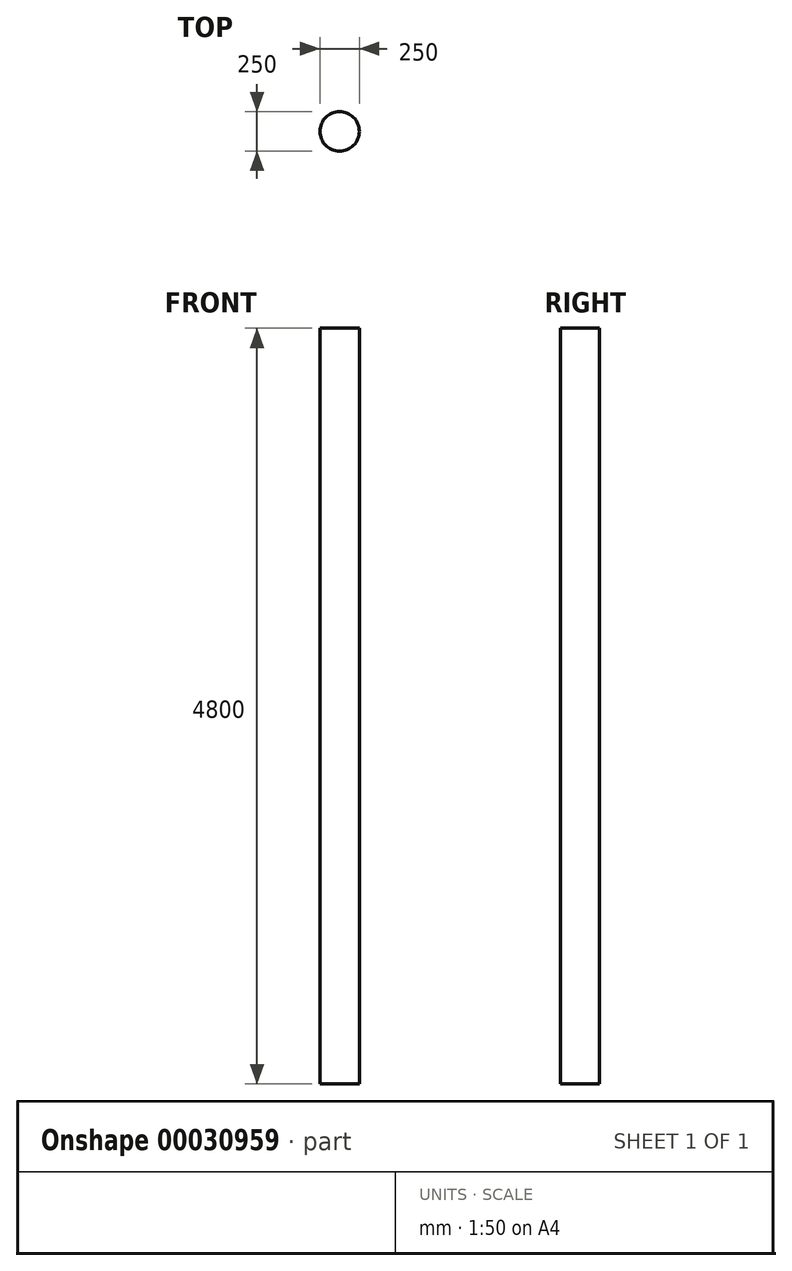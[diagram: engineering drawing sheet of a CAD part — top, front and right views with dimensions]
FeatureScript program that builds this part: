
annotation { "Feature Type Name" : "Feature", "Feature Type Description" : "" }
export const myFeature = defineFeature(function(context is Context, id is Id, definition is map)
    precondition{}
    {
        {
            var Q0;
            Q0=qCreatedBy(makeId("Top.planeOp"),FACE);
            var sketch = newSketch(context, id + "F0", { "sketchPlane" : qUnion([Q0])});
            skCircle(sketch, "E0", {"center": v(0, 0) * mm, "radius": 125 * mm});
            skSolve(sketch);
        }
        {
            var Q0;
            Q0 = qSketchRegion(id + "F0", true);
            extrude(context, id + "F1", {"entities" : qUnion([Q0]), "depth" : 4800 * mm});
        }
    });
